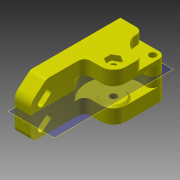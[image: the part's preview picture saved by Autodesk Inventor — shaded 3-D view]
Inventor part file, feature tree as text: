
AUTODESK INVENTOR PART (.ipt)
format: ipt  version: 2013 (Build 170138000, 138)  size: 171,008 bytes
history: native  units: mm
features: other x3, plane x1
ambient origin geometry x8: Origin, YZ Plane, XZ Plane, XY Plane, X Axis, Y Axis, Z Axis, Center Point
bodies: Solid1 (feature_tree)
feature tree (4):
  other  "ARM.ipt"
  other  "Solid1::ARM.ipt"
  other  "TaggingFeature1"
  plane  "Work Plane1"
